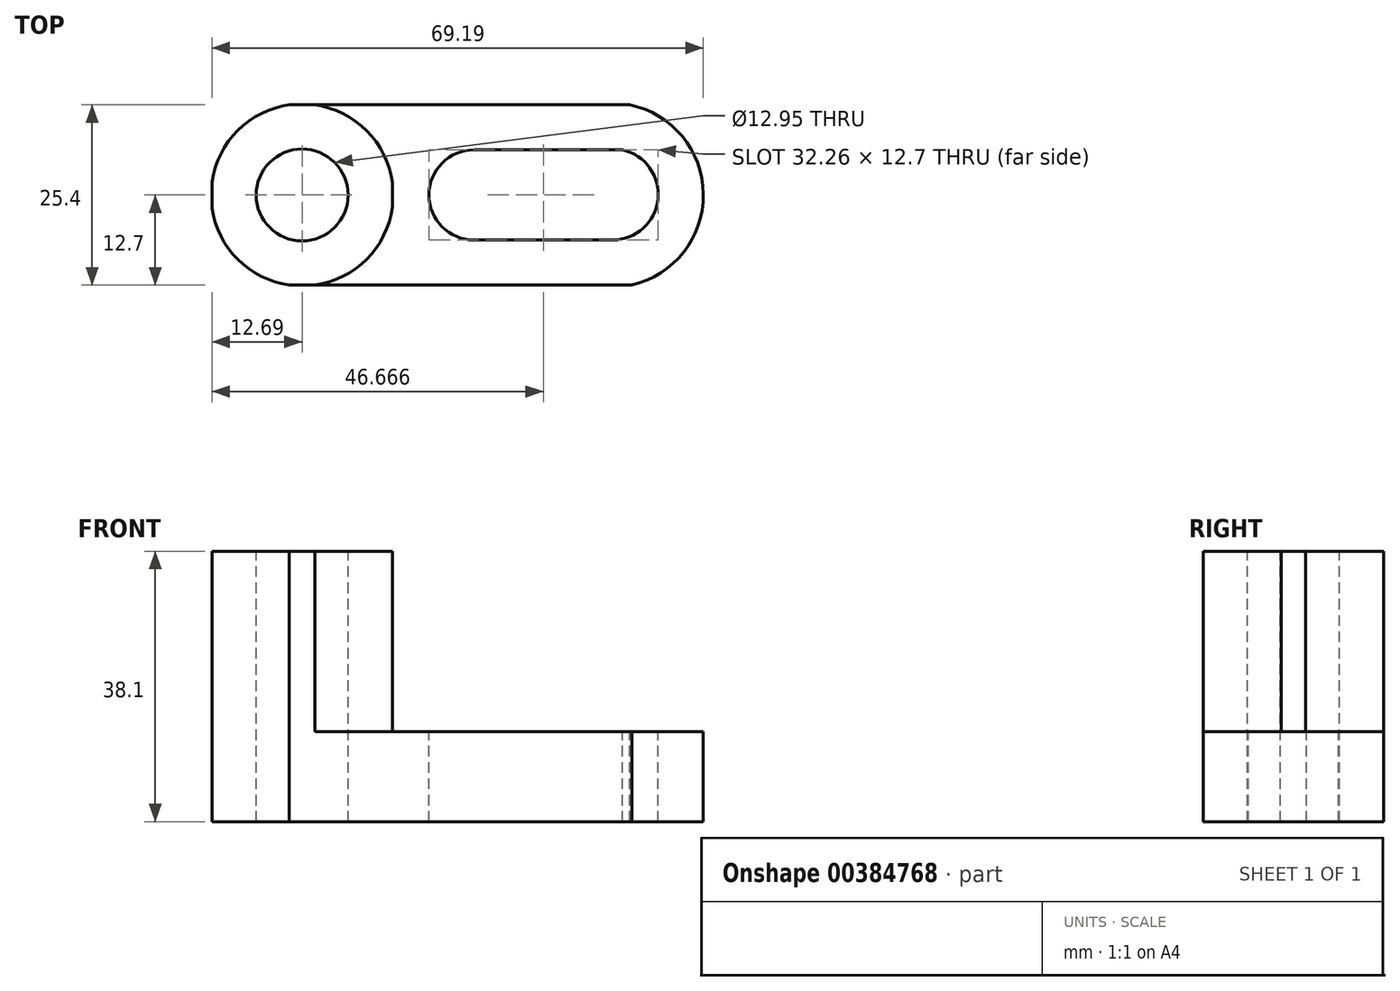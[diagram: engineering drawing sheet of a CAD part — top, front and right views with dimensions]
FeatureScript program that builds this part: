
annotation { "Feature Type Name" : "Feature", "Feature Type Description" : "" }
export const myFeature = defineFeature(function(context is Context, id is Id, definition is map)
    precondition{}
    {
        {
            var Q0;
            Q0=qCreatedBy(makeId("Front.planeOp"),FACE);
            var sketch = newSketch(context, id + "F0", { "sketchPlane" : qUnion([Q0])});
            skLineSegment(sketch, "E0", {"start": v(0, 38.1) * mm, "end": v(0, 0) * mm});
            skLineSegment(sketch, "E1", {"start": v(0, 0) * mm, "end": v(69.85, 0) * mm});
            skLineSegment(sketch, "E2", {"start": v(69.85, 0) * mm, "end": v(69.85, 12.7) * mm});
            skLineSegment(sketch, "E3", {"start": v(69.85, 12.7) * mm, "end": v(25.4, 12.7) * mm});
            skLineSegment(sketch, "E4", {"start": v(25.4, 12.7) * mm, "end": v(25.4, 38.1) * mm});
            skLineSegment(sketch, "E5", {"start": v(25.4, 38.1) * mm, "end": v(0, 38.1) * mm});
            skSolve(sketch);
        }
        {
            var Q0;
            Q0 = qSketchRegion(id + "F0", true);
            extrude(context, id + "F1", {"entities" : qUnion([Q0]), "depth" : 25.4 * mm});
        }
        {
            var Q0;
            Q0=makeQuery(id+"F1.opExtrude","SWEPT_FACE",FACE,{"disambiguationData":[OSD([sQuery(id+"F0.wireOp",EDGE,"E3")])]});
            var sketch = newSketch(context, id + "F2", { "sketchPlane" : qUnion([Q0])});
            skArc(sketch, "E6", {"start": v(59.12, -25.4) * mm, "mid": v(69.19, -12.58) * mm, "end": v(58.8, 0) * mm});
            skSolve(sketch);
        }
        {
            var Q0;
            {var subQ0=sQuery(id+"F2.wireOp",EDGE,"E6");Q0=makeQuery(id+"F2.imprint","IMPRINT",FACE,{"disambiguationData":[TD([[makeQuery(id+"F2.imprint","IMPRINT",EDGE,{"derivedFrom":subQ0}),-1.0]])]});}
            extrude(context, id + "F3", {"entities" : qUnion([Q0]), "operationType" : NewBodyOperationType.REMOVE, "oppositeDirection" : true, "depth" : 25.4 * mm});
        }
        {
            var Q0;
            Q0=makeQuery(id+"F1.opExtrude","SWEPT_FACE",FACE,{"disambiguationData":[OSD([sQuery(id+"F0.wireOp",EDGE,"E3")])]});
            var sketch = newSketch(context, id + "F4", { "sketchPlane" : qUnion([Q0])});
            skLineSegment(sketch, "E7", {"start": v(36.88, -6.35) * mm, "end": v(57.8, -6.35) * mm});
            skLineSegment(sketch, "E8", {"start": v(36.88, -19.05) * mm, "end": v(56.4, -19.05) * mm});
            skArc(sketch, "E9", {"start": v(36.88, -6.35) * mm, "mid": v(30.53, -12.7) * mm, "end": v(36.88, -19.05) * mm});
            skArc(sketch, "E10", {"start": v(56.4, -19.05) * mm, "mid": v(62.8, -13.33) * mm, "end": v(57.8, -6.35) * mm});
            skSolve(sketch);
        }
        {
            var Q0;
            Q0=makeQuery(id+"F4.imprint","IMPRINT",FACE,{"disambiguationData":[TD([[makeQuery(id+"F4.imprint","IMPRINT",EDGE,{"derivedFrom":sQuery(id+"F4.wireOp",EDGE,"E7")}),-1.0]])]});
            extrude(context, id + "F5", {"entities" : qUnion([Q0]), "operationType" : NewBodyOperationType.REMOVE, "oppositeDirection" : true, "depth" : 25.4 * mm});
        }
        {
            var Q0;
            Q0=makeQuery(id+"F1.opExtrude","SWEPT_FACE",FACE,{"disambiguationData":[OSD([sQuery(id+"F0.wireOp",EDGE,"E5")])]});
            var sketch = newSketch(context, id + "F6", { "sketchPlane" : qUnion([Q0])});
            skCircle(sketch, "E11", {"center": v(12.7, -12.7) * mm, "radius": 12.83 * mm});
            skPoint(sketch, "E11.centerSnap0", {"position": v(25.4, -12.7) * mm});
            skSolve(sketch);
        }
        {
            var Q0;
            {var subQ0=sQuery(id+"F6.wireOp",EDGE,"E11");var subQ1=sQuery(id+"F0.wireOp",EDGE,"E5");var subQ2=makeQuery(id+"F1.opExtrude","CAP_EDGE",EDGE,{"disambiguationData":[OSD([subQ1])],"isStart":true});var subQ3=makeQuery(id+"F6.imprint","INTERSECT",VERTEX,{"disambiguationData":[OD(0.0)],"derivedFrom":[subQ2,subQ0]});Q0=makeQuery(id+"F6.imprint","IMPRINT",FACE,{"disambiguationData":[TD([[makeQuery(id+"F6.imprint","IMPRINT",EDGE,{"disambiguationData":[TD([[subQ3,1.0]])],"derivedFrom":subQ0}),-1.0]])]});}
            var Q1;
            {var subQ0=sQuery(id+"F6.wireOp",EDGE,"E11");var subQ1=sQuery(id+"F0.wireOp",EDGE,"E5");var subQ2=makeQuery(id+"F1.opExtrude","CAP_EDGE",EDGE,{"disambiguationData":[OSD([subQ1])],"isStart":true});var subQ3=makeQuery(id+"F6.imprint","INTERSECT",VERTEX,{"disambiguationData":[OD(1.0)],"derivedFrom":[subQ2,subQ0]});Q1=makeQuery(id+"F6.imprint","IMPRINT",FACE,{"disambiguationData":[TD([[makeQuery(id+"F6.imprint","IMPRINT",EDGE,{"disambiguationData":[TD([[subQ3,-1.0]])],"derivedFrom":subQ0}),-1.0]])]});}
            var Q2;
            {var subQ0=sQuery(id+"F6.wireOp",EDGE,"E11");var subQ1=sQuery(id+"F0.wireOp",EDGE,"E5");var subQ4=makeQuery(id+"F1.opExtrude","CAP_EDGE",EDGE,{"disambiguationData":[OSD([subQ1])],"isStart":false});var subQ5=makeQuery(id+"F6.imprint","INTERSECT",VERTEX,{"disambiguationData":[OD(0.0)],"derivedFrom":[subQ4,subQ0]});Q2=makeQuery(id+"F6.imprint","IMPRINT",FACE,{"disambiguationData":[TD([[makeQuery(id+"F6.imprint","IMPRINT",EDGE,{"disambiguationData":[TD([[subQ5,1.0]])],"derivedFrom":subQ0}),-1.0]])]});}
            var Q3;
            {var subQ0=sQuery(id+"F6.wireOp",EDGE,"E11");var subQ1=sQuery(id+"F0.wireOp",EDGE,"E5");var subQ2=makeQuery(id+"F1.opExtrude","CAP_EDGE",EDGE,{"disambiguationData":[OSD([subQ1])],"isStart":false});var subQ3=makeQuery(id+"F6.imprint","INTERSECT",VERTEX,{"disambiguationData":[OD(1.0)],"derivedFrom":[subQ2,subQ0]});Q3=makeQuery(id+"F6.imprint","IMPRINT",FACE,{"disambiguationData":[TD([[makeQuery(id+"F6.imprint","IMPRINT",EDGE,{"disambiguationData":[TD([[subQ3,-1.0]])],"derivedFrom":subQ0}),-1.0]])]});}
            extrude(context, id + "F7", {"entities" : qUnion([Q0, Q1, Q2, Q3]), "operationType" : NewBodyOperationType.REMOVE, "oppositeDirection" : true, "depth" : 25.4 * mm});
        }
        {
            var Q0;
            {var subQ0=sQuery(id+"F0.wireOp",EDGE,"E5");var subQ1=makeQuery(id+"F1.opExtrude","CAP_EDGE",EDGE,{"disambiguationData":[OSD([subQ0])],"isStart":true});var subQ2=sQuery(id+"F0.wireOp",EDGE,"E0");var subQ3=makeQuery(id+"F1.opExtrude","SWEPT_EDGE",EDGE,{"disambiguationData":[OSD([subQ2,subQ0])]});var subQ4=makeQuery(id+"F6.imprint","INTERSECT",VERTEX,{"derivedFrom":[subQ3,subQ1]});var subQ5=sQuery(id+"F6.wireOp",EDGE,"E11");var subQ6=makeQuery(id+"F6.imprint","INTERSECT",VERTEX,{"disambiguationData":[OD(1.0)],"derivedFrom":[subQ1,subQ5]});Q0=makeQuery(id+"F7.boolean.opBoolean","COPY",FACE,{"derivedFrom":makeQuery(id+"F7.opExtrude","CAP_FACE",FACE,{"disambiguationData":[OSD([subQ2,subQ0,subQ5]),TDD([makeQuery(id+"F6.imprint","IMPRINT",EDGE,{"disambiguationData":[TD([[subQ6,-1.0]])],"derivedFrom":subQ5}),makeQuery(id+"F6.imprint","IMPRINT",EDGE,{"disambiguationData":[TD([[subQ4,1.0]])],"derivedFrom":subQ3}),makeQuery(id+"F6.imprint","IMPRINT",EDGE,{"disambiguationData":[TD([[subQ6,-1.0]])],"derivedFrom":subQ1})])],"isStart":false})});}
            var Q1;
            {var subQ0=sQuery(id+"F0.wireOp",EDGE,"E5");var subQ1=makeQuery(id+"F1.opExtrude","CAP_EDGE",EDGE,{"disambiguationData":[OSD([subQ0])],"isStart":false});var subQ2=sQuery(id+"F0.wireOp",EDGE,"E0");var subQ3=makeQuery(id+"F1.opExtrude","SWEPT_EDGE",EDGE,{"disambiguationData":[OSD([subQ2,subQ0])]});var subQ4=makeQuery(id+"F6.imprint","INTERSECT",VERTEX,{"derivedFrom":[subQ3,subQ1]});var subQ5=sQuery(id+"F6.wireOp",EDGE,"E11");var subQ6=makeQuery(id+"F6.imprint","INTERSECT",VERTEX,{"disambiguationData":[OD(0.0)],"derivedFrom":[subQ1,subQ5]});Q1=makeQuery(id+"F7.boolean.opBoolean","COPY",FACE,{"derivedFrom":makeQuery(id+"F7.opExtrude","CAP_FACE",FACE,{"disambiguationData":[OSD([subQ2,subQ0,subQ5]),TDD([makeQuery(id+"F6.imprint","IMPRINT",EDGE,{"disambiguationData":[TD([[subQ6,1.0]])],"derivedFrom":subQ5}),makeQuery(id+"F6.imprint","IMPRINT",EDGE,{"disambiguationData":[TD([[subQ4,-1.0]])],"derivedFrom":subQ3}),makeQuery(id+"F6.imprint","IMPRINT",EDGE,{"disambiguationData":[TD([[subQ6,-1.0]])],"derivedFrom":subQ1})])],"isStart":false})});}
            extrude(context, id + "F8", {"entities" : qUnion([Q0, Q1]), "operationType" : NewBodyOperationType.REMOVE, "oppositeDirection" : true, "depth" : 25.4 * mm});
        }
        {
            var Q0;
            Q0=makeQuery(id+"F1.opExtrude","SWEPT_FACE",FACE,{"disambiguationData":[OSD([sQuery(id+"F0.wireOp",EDGE,"E5")])]});
            var sketch = newSketch(context, id + "F9", { "sketchPlane" : qUnion([Q0])});
            skCircle(sketch, "E12", {"center": v(12.7, -12.7) * mm, "radius": 6.48 * mm});
            skSolve(sketch);
        }
        {
            var Q0;
            Q0=makeQuery(id+"F9.imprint","IMPRINT",FACE,{"disambiguationData":[TD([[makeQuery(id+"F9.imprint","IMPRINT",EDGE,{"derivedFrom":sQuery(id+"F9.wireOp",EDGE,"E12")}),1.0]])]});
            extrude(context, id + "F10", {"entities" : qUnion([Q0]), "operationType" : NewBodyOperationType.REMOVE, "oppositeDirection" : true, "depth" : 40.64 * mm});
        }
    });
